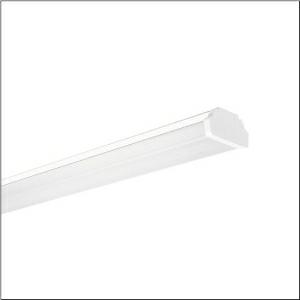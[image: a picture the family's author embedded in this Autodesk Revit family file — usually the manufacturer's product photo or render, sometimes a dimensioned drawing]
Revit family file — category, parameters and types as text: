
# Revit family: dus_r__31_gen_2_53bd8127v485c2_ffde
name_source: partatom
category: Lighting Fixtures
units: mm (PartAtom-declared; Revit-internal decimal feet)

## family parameters
Cut with Voids When Loaded = No
Host = Face
Light Source = No
Part Type = Normal
Room Calculation Point = No
Round Connector Dimension = Use Diameter
Shared = No

## types (1)
- DUS® 31 Gen.2 (1 x LED, 8590 lm, 47.9 W, 4000K)
    Apparent Load = 48 VA
    CIE Flux Codes = 47 80 95 93 100
    Color Rendering = 80
    Color Temperature = 4000K
    Default Elevation = 1800 mm
    Description = DUS® 31 Gen.2, luminaire insert, of sheet steel, coil coated, white, length: 1.535mm, width: 81mm, height: 90mm, 5x system unit, system units: 307mm, LED rated luminous flux: 8.590lm, light colour: 840, control gear: ON/OFF, control gear: ECG, with plug, 3-pole, with phase selection, mains connection: 220..240V, AC, 50/60Hz, rated input power: 48W, through-wiring accessed according to module size, primary optical cover: cover, of PMMA, light emission: direct distribution, primary light characteristic: symmetric, protection rating (complete): IP20, protection rating (LED compartment): IP50, insulation class (complete): insulation class I (protective earthing), certification: CE, ENEC, VDE, UKCA, impact resistance: IK03, permissible ambient temperature for indoor applications: -35..+45°C, corresponds to IFS (International Featured Standards) requirements for safety and quality in the food industry, reducing of maximum allowable ambient temperature of 5°C with ceiling mounting, packaging unit: 1 piece
    Height = 95 mm
    Lamp = 1 x LED
    Lamp Light Flux = 8590 lm
    Lamp Power = 47.9 W
    Lamp count = 1
    Length = 1535 mm
    Luminous efficacy = 179 lm/W
    Manufacturer = Siteco
    ModVariant = No
    Model = 53BD8127V485C2
    Mounting Place = Ceiling
    Mounting Type = Pendant
    Number of Poles = 1
    OnlyDefault = Yes
    Power Factor = 1
    Product Name = DUS® 31 Gen.2
    Product group = luminaire insert
    ProductGroupID = 902
    Protection Class = Protection class I
    Protection Degree = IP 20
    RLX_Detail_Level = 1
    RLX_Emergency_Light_Flux = 0 lm
    RLX_Emergency_Type = 0
    RLX_Emergency_Type_DB = No
    RlxData = <blob elided: 28401 chars, md5=b19c7a3d>
    Socket = socket
    Standby Power = 0 W
    System Light Flux = 8590 lm
    System Power = 48 W
    Type Comments = Product without accessories
    Type Image = l_1319596.jpg
    URL = http://relux.com
    VarID = ---
    Voltage = 0 V
    Weight = 0.00 kg
    Width = 81 mm

## geometry (parser evidence)
native form markers: Blend x4, Sweep x12
no freeform markers — native parametric forms only
